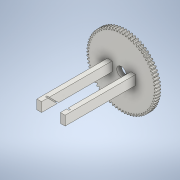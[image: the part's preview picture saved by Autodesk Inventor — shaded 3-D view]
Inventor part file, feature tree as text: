
AUTODESK INVENTOR PART (.ipt)
format: ipt  version: 2022.2 (Build 262287010, 287A)  size: 531,968 bytes
history: native  units: mm (DEFAULTED — no unit token found)
features: sketch x9, extrude x8, plane x3, other x3, mirror x1
ambient origin geometry x8: Origin, YZ Plane, XZ Plane, XY Plane, X Axis, Y Axis, Z Axis, Center Point
bodies: Solid1 (feature_tree)
feature tree (24):
  extrude  "Extrusion1"  Depth=10.0mm TaperAngle=0.0deg
  plane  "Work Plane2"
  plane  "Work Plane8"
  plane  "Work Plane9"
  other  "Engranaje recto"
  extrude  "Extrusión2"  Depth=10.0mm TaperAngle=0.0deg
  extrude  "Extrusión4"  Depth=0.436332mm TaperAngle=0.0deg
  extrude  "Extrusión7"  TaperAngle=0.0deg  [1 undecoded]
  mirror  "Simetría1"
  extrude  "Extrusión9"  Depth=90.0mm
  extrude  "Extrusión10"  Depth=20.0mm
  extrude  "Extrusión11"  Depth=25.0mm
  extrude  "Extrusión12"  Depth=20.0mm
  sketch  "Boceto13"  dims[d60=150.0mm d61=0.0mm d84=5.0mm d85=0.0mm d86=130.0mm d87=1.5mm d93=5.0mm d94=1.0mm d95=0.0mm d96=40.0mm d97=25.0mm d99=55.0mm d100=3.0mm d101=0.0mm d102=75.0mm d103=55.0mm d104=3.0mm d105=0.0mm d106=40.0mm d107=3.0mm d108=0.0mm d109=0.5mm d110=0.872665mm]
  sketch  "Sketch1"  dims[d0=148.0mm d1=10.0mm d2=0.0mm]
  sketch  "Sketch2"  dims[d3=144.0mm d4=10.0mm d5=0.0mm]
  other  "Srf1"
  sketch  "Boceto3"  dims[d16=90.0mm d17=0.0mm d34=0.436332mm]
  sketch  "Boceto5"  dims[d39=0.0mm d41=0.0mm]
  sketch  "Boceto9"  dims[d43=90.0mm d46=90.0mm]
  sketch  "Boceto10"  dims[d47=0.0mm d48=0.0mm d49=20.0mm]
  sketch  "Boceto11"  dims[d50=0.0mm d51=0.0mm d54=25.0mm]
  sketch  "Boceto12"  dims[d58=10.0mm d59=20.0mm]
  other  "Diámetro de separación"
note: 1 required parameter value undecoded (feature->parameter linkage not recoverable at this tier; creation-order binding heuristic only, values carry confidence <= 0.55)
